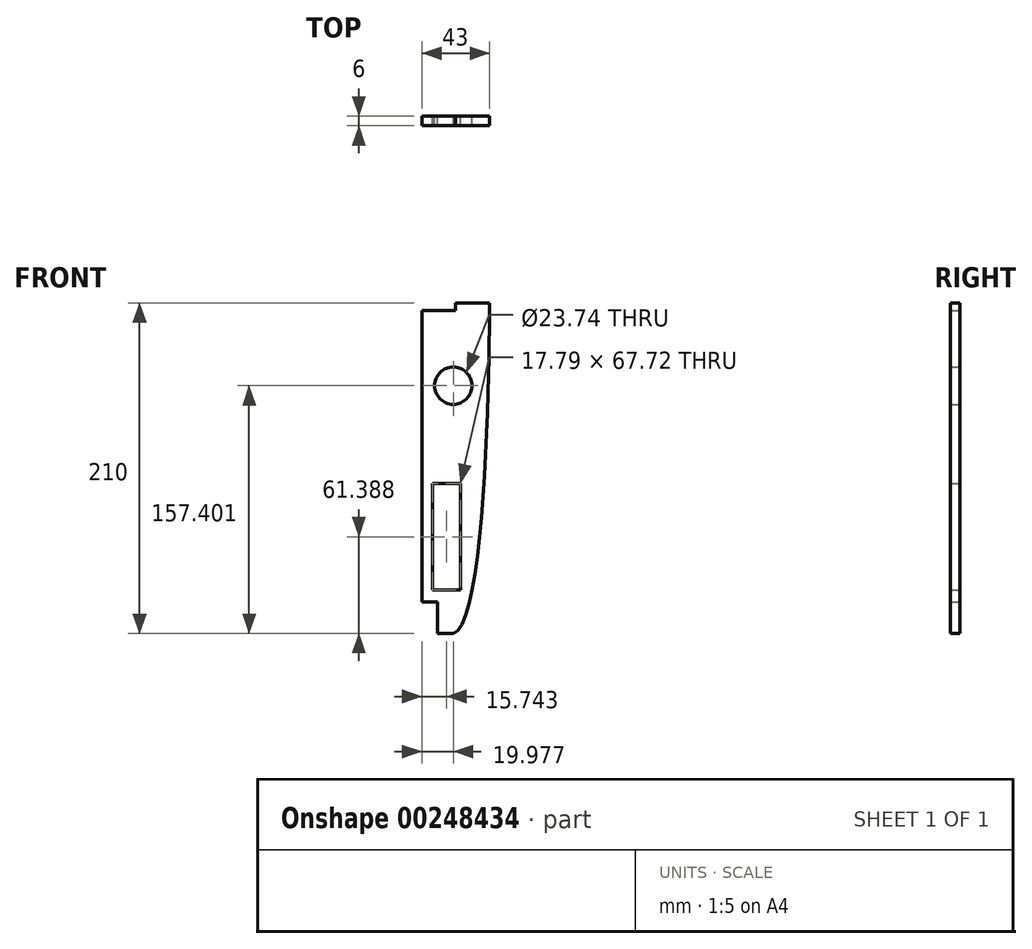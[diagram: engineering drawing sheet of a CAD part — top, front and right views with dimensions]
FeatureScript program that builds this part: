
annotation { "Feature Type Name" : "Feature", "Feature Type Description" : "" }
export const myFeature = defineFeature(function(context is Context, id is Id, definition is map)
    precondition{}
    {
        {
            var Q0;
            Q0=qCreatedBy(makeId("Front.planeOp"),FACE);
            var sketch = newSketch(context, id + "F0", { "sketchPlane" : qUnion([Q0])});
            skFitSpline(sketch, "E0", {"points": [v(155.76, 291.87) * mm, v(178.76, 81.87) * mm], "startDerivative": vector(69.02, -18) * mm, "endDerivative": vector(-0.02, -2.14) * mm});
            skLineSegment(sketch, "E1", {"start": v(178.76, 81.87) * mm, "end": v(135.76, 81.87) * mm});
            skLineSegment(sketch, "E2", {"start": v(178.77, 291.87) * mm, "end": v(178.77, 82.58) * mm});
            skLineSegment(sketch, "E3.bottom", {"start": v(160.4, 264.34) * mm, "end": v(142.6, 264.34) * mm});
            skLineSegment(sketch, "E3.top", {"start": v(160.4, 196.62) * mm, "end": v(142.6, 196.62) * mm});
            skLineSegment(sketch, "E3.left", {"start": v(160.4, 264.34) * mm, "end": v(160.4, 196.62) * mm});
            skLineSegment(sketch, "E3.right", {"start": v(142.6, 264.34) * mm, "end": v(142.6, 196.62) * mm});
            skCircle(sketch, "E4", {"center": v(155.74, 134.46) * mm, "radius": 11.87 * mm});
            skLineSegment(sketch, "E5.MirrorCS", {"start": v(160.4, -100.6) * mm, "end": v(142.6, -100.6) * mm});
            skFitSpline(sketch, "E6.MirrorCS", {"points": [v(155.76, -128.13) * mm, v(178.76, 81.87) * mm], "startDerivative": vector(69.02, 18) * mm, "endDerivative": vector(-0.02, 2.14) * mm});
            skLineSegment(sketch, "E7.MirrorCS", {"start": v(142.6, -100.6) * mm, "end": v(142.6, -32.88) * mm});
            skLineSegment(sketch, "E8.MirrorCS", {"start": v(160.4, -100.6) * mm, "end": v(160.4, -32.88) * mm});
            skLineSegment(sketch, "E9.MirrorCS", {"start": v(178.77, -128.13) * mm, "end": v(178.77, 81.16) * mm});
            skLineSegment(sketch, "E10.MirrorCS", {"start": v(160.4, -32.88) * mm, "end": v(142.6, -32.88) * mm});
            skCircle(sketch, "E11.MirrorC", {"center": v(155.74, 29.27) * mm, "radius": 11.87 * mm});
            skLineSegment(sketch, "E12", {"start": v(157.26, 81.87) * mm, "end": v(157.26, 86.87) * mm});
            skLineSegment(sketch, "E13", {"start": v(157.26, 81.87) * mm, "end": v(157.26, 76.87) * mm});
            skLineSegment(sketch, "E14", {"start": v(157.26, 86.87) * mm, "end": v(135.76, 86.87) * mm});
            skLineSegment(sketch, "E15", {"start": v(157.26, 76.87) * mm, "end": v(135.76, 76.87) * mm});
            skLineSegment(sketch, "E16", {"start": v(145.76, 291.87) * mm, "end": v(145.76, 271.87) * mm});
            skLineSegment(sketch, "E17", {"start": v(145.76, 271.87) * mm, "end": v(135.76, 271.87) * mm});
            skLineSegment(sketch, "E18", {"start": v(145.76, 291.87) * mm, "end": v(155.76, 291.87) * mm});
            skLineSegment(sketch, "E19", {"start": v(135.76, 271.87) * mm, "end": v(135.76, 81.87) * mm});
            skLineSegment(sketch, "E20", {"start": v(155.76, 291.87) * mm, "end": v(178.77, 291.87) * mm});
            skLineSegment(sketch, "E21.MirrorCS", {"start": v(145.76, -128.13) * mm, "end": v(145.76, -108.13) * mm});
            skLineSegment(sketch, "E22.MirrorCS", {"start": v(145.76, -108.13) * mm, "end": v(135.76, -108.13) * mm});
            skLineSegment(sketch, "E23", {"start": v(145.76, -128.13) * mm, "end": v(155.76, -128.13) * mm});
            skLineSegment(sketch, "E24", {"start": v(135.76, -108.13) * mm, "end": v(135.76, 81.87) * mm});
            skLineSegment(sketch, "E25", {"start": v(178.77, -128.13) * mm, "end": v(155.76, -128.13) * mm});
            skSolve(sketch);
        }
        {
            var Q0;
            Q0=makeQuery(id+"F0.imprint","IMPRINT",FACE,{"disambiguationData":[TD([[makeQuery(id+"F0.imprint","IMPRINT",EDGE,{"derivedFrom":sQuery(id+"F0.wireOp",EDGE,"85cddfad-3993-4289-a329-3e50ecc5d13c")}),-1.0]])]});
            var Q1;
            Q1=makeQuery(id+"F0.imprint","IMPRINT",FACE,{"disambiguationData":[TD([[makeQuery(id+"F0.imprint","IMPRINT",EDGE,{"derivedFrom":sQuery(id+"F0.wireOp",EDGE,"E5.MirrorCS")}),1.0]])]});
            extrude(context, id + "F1", {"entities" : qUnion([Q0, Q1]), "depth" : 6 * mm});
        }
    });
